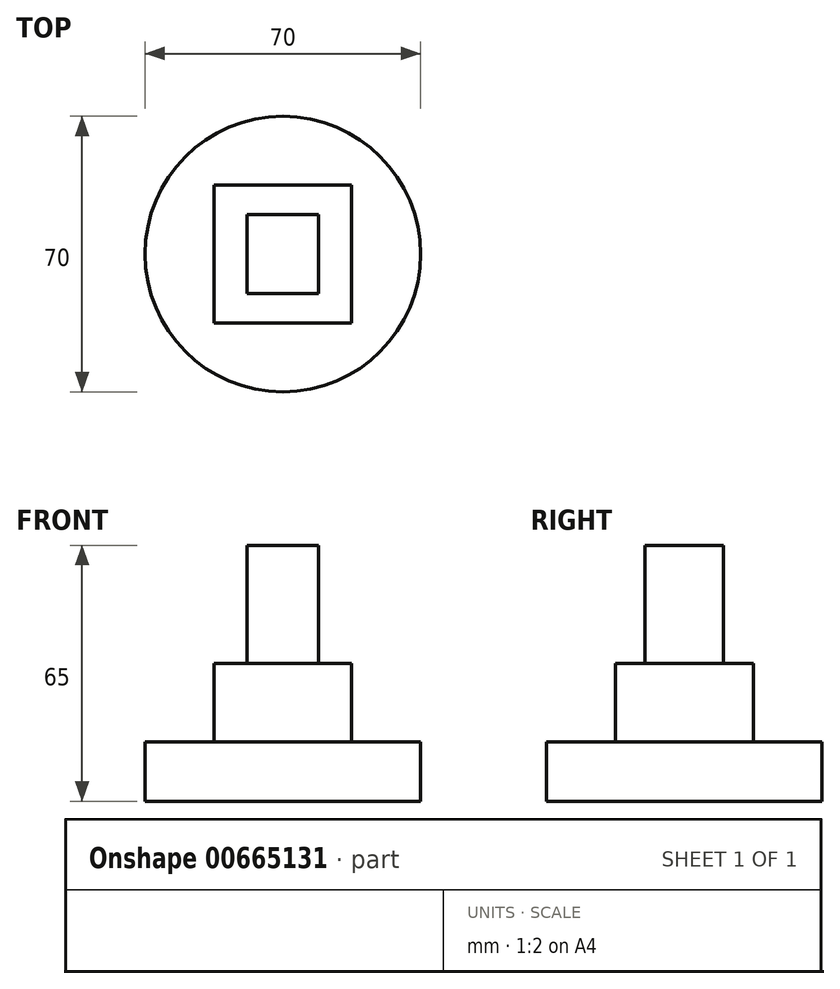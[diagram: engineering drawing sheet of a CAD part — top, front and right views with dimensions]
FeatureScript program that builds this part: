
annotation { "Feature Type Name" : "Feature", "Feature Type Description" : "" }
export const myFeature = defineFeature(function(context is Context, id is Id, definition is map)
    precondition{}
    {
        {
            var Q0;
            Q0=qCreatedBy(makeId("Top.planeOp"),FACE);
            var sketch = newSketch(context, id + "F0", { "sketchPlane" : qUnion([Q0])});
            skCircle(sketch, "E0", {"center": v(0, 0) * mm, "radius": 35 * mm});
            skSolve(sketch);
        }
        {
            var Q0;
            Q0 = qSketchRegion(id + "F0", true);
            extrude(context, id + "F1", {"entities" : qUnion([Q0]), "depth" : 15 * mm, "offsetDistance" : 25.4 * mm});
        }
        {
            var Q0;
            Q0=makeQuery(id+"F1.opExtrude","CAP_FACE",FACE,{"disambiguationData":[OSD([sQuery(id+"F0.wireOp",EDGE,"E0")])],"isStart":false});
            var sketch = newSketch(context, id + "F2", { "sketchPlane" : qUnion([Q0])});
            skLineSegment(sketch, "E1.bottom", {"start": v(-17.5, 17.5) * mm, "end": v(17.5, 17.5) * mm});
            skLineSegment(sketch, "E1.top", {"start": v(-17.5, -17.5) * mm, "end": v(17.5, -17.5) * mm});
            skLineSegment(sketch, "E1.left", {"start": v(-17.5, 17.5) * mm, "end": v(-17.5, -17.5) * mm});
            skLineSegment(sketch, "E1.right", {"start": v(17.5, 17.5) * mm, "end": v(17.5, -17.5) * mm});
            skPoint(sketch, "E1.middle", {"position": v(0, 0) * mm});
            skSolve(sketch);
        }
        {
            var Q0;
            Q0 = qSketchRegion(id + "F2", true);
            extrude(context, id + "F3", {"entities" : qUnion([Q0]), "operationType" : NewBodyOperationType.ADD, "depth" : 20 * mm, "offsetDistance" : 25.4 * mm});
        }
        {
            var Q0;
            Q0=makeQuery(id+"F3.opExtrude","CAP_FACE",FACE,{"disambiguationData":[OSD([sQuery(id+"F2.wireOp",EDGE,"E1.bottom"),sQuery(id+"F2.wireOp",EDGE,"E1.top"),sQuery(id+"F2.wireOp",EDGE,"E1.left"),sQuery(id+"F2.wireOp",EDGE,"E1.right")])],"isStart":false});
            var sketch = newSketch(context, id + "F4", { "sketchPlane" : qUnion([Q0])});
            skLineSegment(sketch, "E2.bottom", {"start": v(9.1, 10) * mm, "end": v(-9.1, 10) * mm});
            skLineSegment(sketch, "E2.top", {"start": v(9.1, -10) * mm, "end": v(-9.1, -10) * mm});
            skLineSegment(sketch, "E2.left", {"start": v(9.1, 10) * mm, "end": v(9.1, -10) * mm});
            skLineSegment(sketch, "E2.right", {"start": v(-9.1, 10) * mm, "end": v(-9.1, -10) * mm});
            skPoint(sketch, "E2.middle", {"position": v(0, 0) * mm});
            skSolve(sketch);
        }
        {
            var Q0;
            Q0 = qSketchRegion(id + "F4", true);
            extrude(context, id + "F5", {"entities" : qUnion([Q0]), "operationType" : NewBodyOperationType.ADD, "depth" : 30 * mm, "offsetDistance" : 25.4 * mm});
        }
    });
